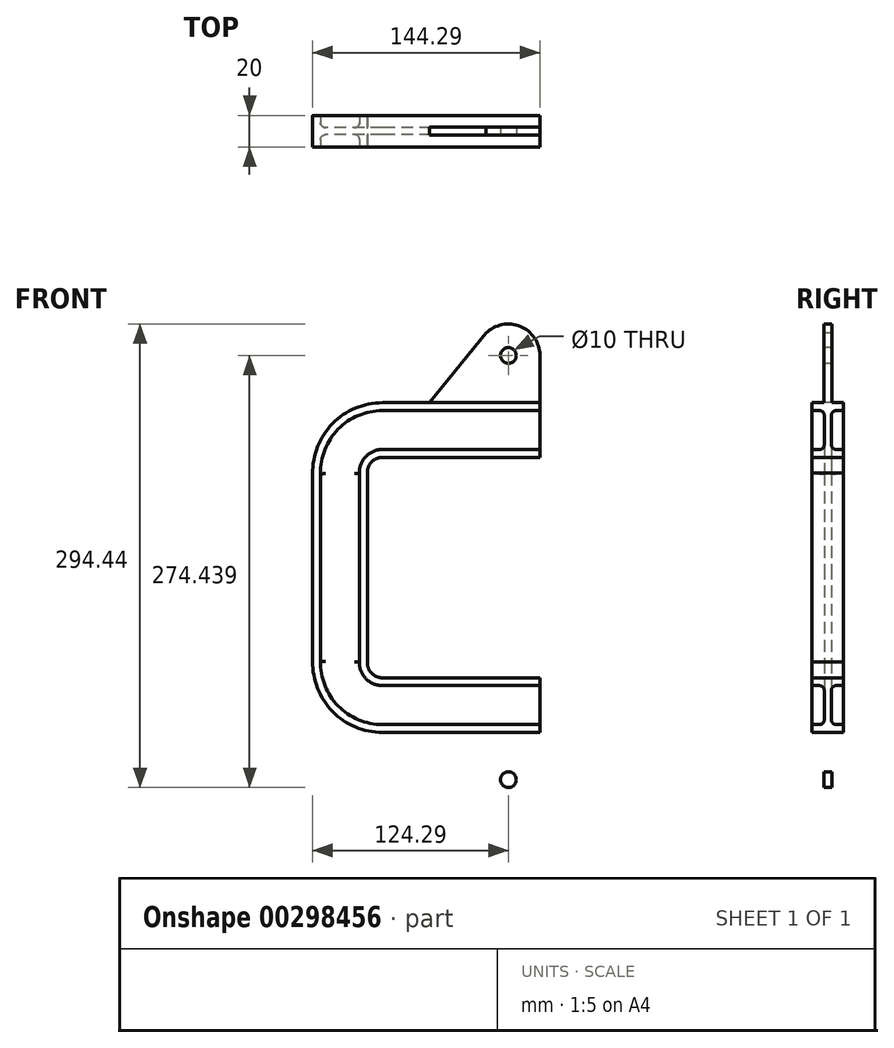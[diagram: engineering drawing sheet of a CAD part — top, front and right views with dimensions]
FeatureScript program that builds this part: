
annotation { "Feature Type Name" : "Feature", "Feature Type Description" : "" }
export const myFeature = defineFeature(function(context is Context, id is Id, definition is map)
    precondition{}
    {
        {
            var Q0;
            Q0=qCreatedBy(makeId("Front.planeOp"),FACE);
            var sketch = newSketch(context, id + "F0", { "sketchPlane" : qUnion([Q0])});
            skLineSegment(sketch, "E0", {"start": v(0, 70.43) * mm, "end": v(-100, 70.43) * mm});
            skArc(sketch, "E1", {"start": v(-100, 70.43) * mm, "mid": v(-107.22, 67.35) * mm, "end": v(-110, 60) * mm});
            skLineSegment(sketch, "E2", {"start": v(-110, 60) * mm, "end": v(-110, 0) * mm});
            skLineSegment(sketch, "E3.MirrorCS", {"start": v(0, -70.43) * mm, "end": v(-100, -70.43) * mm});
            skLineSegment(sketch, "E4.MirrorCS", {"start": v(-110, -60) * mm, "end": v(-110, 0) * mm});
            skArc(sketch, "E5.MirrorCS", {"start": v(-100, -70.43) * mm, "mid": v(-107.22, -67.35) * mm, "end": v(-110, -60) * mm});
            skSolve(sketch);
        }
        {
            var Q0;
            Q0=qCreatedBy(makeId("Right.planeOp"),FACE);
            var sketch = newSketch(context, id + "F1", { "sketchPlane" : qUnion([Q0])});
            skLineSegment(sketch, "E6", {"start": v(0, 70) * mm, "end": v(10, 70) * mm});
            skLineSegment(sketch, "E7", {"start": v(10, 70) * mm, "end": v(10, 75) * mm});
            skLineSegment(sketch, "E8", {"start": v(10, 75) * mm, "end": v(5.27, 75) * mm});
            skArc(sketch, "E9", {"start": v(5.27, 75) * mm, "mid": v(3.14, 75.88) * mm, "end": v(2.27, 78) * mm});
            skLineSegment(sketch, "E10", {"start": v(2.27, 78) * mm, "end": v(2.27, 96.72) * mm});
            skArc(sketch, "E11", {"start": v(2.27, 96.72) * mm, "mid": v(3.14, 98.84) * mm, "end": v(5.27, 99.72) * mm});
            skLineSegment(sketch, "E12", {"start": v(5.27, 99.72) * mm, "end": v(10, 99.72) * mm});
            skLineSegment(sketch, "E13", {"start": v(10, 99.72) * mm, "end": v(10, 104.72) * mm});
            skLineSegment(sketch, "E14", {"start": v(10, 104.72) * mm, "end": v(0, 104.72) * mm});
            skLineSegment(sketch, "E15.MirrorCS", {"start": v(-5.27, 99.72) * mm, "end": v(-10, 99.72) * mm});
            skArc(sketch, "E16.MirrorCS", {"start": v(-5.27, 75) * mm, "mid": v(-3.14, 75.88) * mm, "end": v(-2.27, 78) * mm});
            skLineSegment(sketch, "E17.MirrorCS", {"start": v(-10, 75) * mm, "end": v(-5.27, 75) * mm});
            skLineSegment(sketch, "E18.MirrorCS", {"start": v(-10, 99.72) * mm, "end": v(-10, 104.72) * mm});
            skArc(sketch, "E19.MirrorCS", {"start": v(-2.27, 96.72) * mm, "mid": v(-3.14, 98.84) * mm, "end": v(-5.27, 99.72) * mm});
            skLineSegment(sketch, "E20.MirrorCS", {"start": v(-10, 70) * mm, "end": v(-10, 75) * mm});
            skLineSegment(sketch, "E21.MirrorCS", {"start": v(-10, 104.72) * mm, "end": v(0, 104.72) * mm});
            skLineSegment(sketch, "E22.MirrorCS", {"start": v(-2.27, 78) * mm, "end": v(-2.27, 96.72) * mm});
            skLineSegment(sketch, "E23.MirrorCS", {"start": v(0, 70) * mm, "end": v(-10, 70) * mm});
            skSolve(sketch);
        }
        {
            var Q0;
            Q0 = qSketchRegion(id + "F1", true);
            var Q1;
            Q1 = qConstructionFilter(qBodyType(qCreatedBy(id + "F0" ,EDGE), BodyType.WIRE), ConstructionObject.NO);
            sweep(context, id + "F2", {"profiles" : qUnion([Q0]), "path" : qUnion([Q1])});
        }
        {
            var Q0;
            Q0=qCreatedBy(makeId("Front.planeOp"),FACE);
            var sketch = newSketch(context, id + "F3", { "sketchPlane" : qUnion([Q0])});
            skLineSegment(sketch, "E24", {"start": v(0, 104.72) * mm, "end": v(0, 134.72) * mm});
            skLineSegment(sketch, "E25", {"start": v(0, 104.72) * mm, "end": v(-70, 104.72) * mm});
            skArc(sketch, "E26", {"start": v(0, 134.72) * mm, "mid": v(-12.36, 153.2) * mm, "end": v(-34.17, 148.84) * mm});
            skCircle(sketch, "E27", {"center": v(-20, 134.72) * mm, "radius": 5 * mm});
            skLineSegment(sketch, "E28", {"start": v(-34.17, 148.84) * mm, "end": v(-70, 104.72) * mm});
            skCircle(sketch, "E29.MirrorC", {"center": v(-20, -134.72) * mm, "radius": 5 * mm});
            skArc(sketch, "E30.MirrorCS", {"start": v(0, -134.72) * mm, "mid": v(-12.36, -153.2) * mm, "end": v(-34.17, -148.84) * mm});
            skLineSegment(sketch, "E31.MirrorCS", {"start": v(0, -104.72) * mm, "end": v(-70, -104.72) * mm});
            skLineSegment(sketch, "E32.MirrorCS", {"start": v(-34.17, -148.84) * mm, "end": v(-70, -104.72) * mm});
            skLineSegment(sketch, "E33.MirrorCS", {"start": v(0, -104.72) * mm, "end": v(0, -134.72) * mm});
            skSolve(sketch);
        }
        {
            var Q0;
            Q0=makeQuery(id+"F3.imprint","IMPRINT",FACE,{"disambiguationData":[TD([[makeQuery(id+"F3.imprint","IMPRINT",EDGE,{"derivedFrom":sQuery(id+"F3.wireOp",EDGE,"E24")}),1.0]])]});
            var Q1;
            Q1=makeQuery(id+"F3.imprint","IMPRINT",FACE,{"disambiguationData":[TD([[makeQuery(id+"F3.imprint","IMPRINT",EDGE,{"derivedFrom":sQuery(id+"F3.wireOp",EDGE,"E29.MirrorC")}),1.0]])]});
            extrude(context, id + "F4", {"entities" : qUnion([Q0, Q1]), "operationType" : NewBodyOperationType.ADD, "endBound" : BoundingType.SYMMETRIC, "oppositeDirection" : true, "depth" : 5 * mm});
        }
    });
